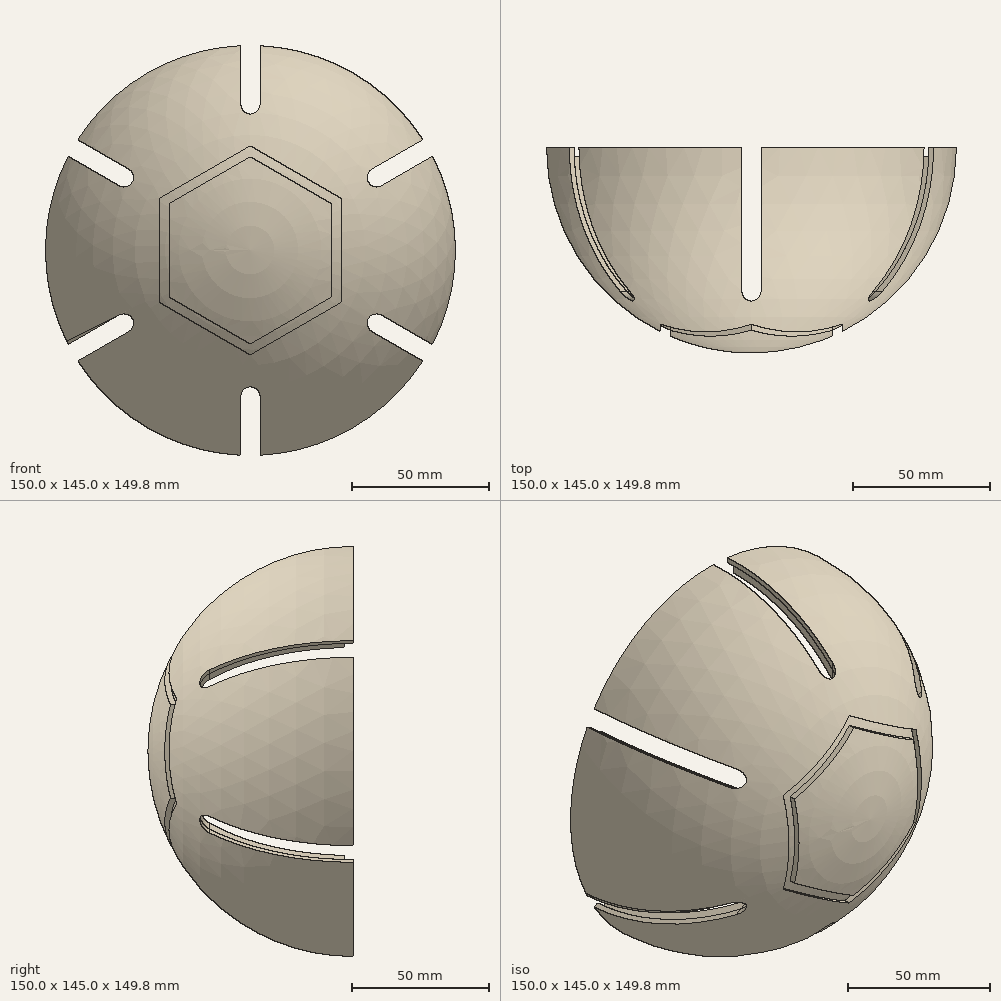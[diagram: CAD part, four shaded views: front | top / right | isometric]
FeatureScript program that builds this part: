
annotation { "Feature Type Name" : "Feature", "Feature Type Description" : "" }
export const myFeature = defineFeature(function(context is Context, id is Id, definition is map)
    precondition{}
    {
        {
            var Q0;
            Q0=qCreatedBy(makeId("Top.planeOp"),FACE);
            var sketch = newSketch(context, id + "F0", { "sketchPlane" : qUnion([Q0])});
            skArc(sketch, "E0", {"start": v(-75, 0) * mm, "mid": v(-53.03, -53.03) * mm, "end": v(0, -75) * mm});
            skLineSegment(sketch, "E1", {"start": v(0, 0) * mm, "end": v(-75, 0) * mm});
            skLineSegment(sketch, "E2", {"start": v(0, 0) * mm, "end": v(0, -75) * mm});
            skSolve(sketch);
        }
        {
            var Q0;
            Q0=makeQuery(id+"F0.imprint","IMPRINT",FACE,{"disambiguationData":[TD([[makeQuery(id+"F0.imprint","IMPRINT",EDGE,{"derivedFrom":sQuery(id+"F0.wireOp",EDGE,"E0")}),1.0]])]});
            var Q1;
            Q1=sQuery(id+"F0.wireOp",EDGE,"E2");
            var Q2;
            Q2=sQuery(id+"F0.wireOp",EDGE,"E2");
            revolve(context, id + "F1", {"entities" : qUnion([Q0]), "surfaceEntities" : qUnion([Q1]), "axis" : qUnion([Q2]), "revolveType" : RevolveType.FULL});
        }
        {
            var Q0;
            Q0=qCreatedBy(makeId("Top.planeOp"),FACE);
            var sketch = newSketch(context, id + "F2", { "sketchPlane" : qUnion([Q0])});
            skLineSegment(sketch, "E3", {"start": v(0, 0) * mm, "end": v(73, 0) * mm});
            skLineSegment(sketch, "E4", {"start": v(0, 0) * mm, "end": v(0, -73) * mm});
            skArc(sketch, "E5", {"start": v(0, -73) * mm, "mid": v(51.62, -51.62) * mm, "end": v(73, 0) * mm});
            skSolve(sketch);
        }
        {
            var Q0;
            Q0 = qSketchRegion(id + "F2", true);
            var Q1;
            Q1=sQuery(id+"F2.wireOp",EDGE,"E4");
            revolve(context, id + "F3", {"operationType" : NewBodyOperationType.REMOVE, "entities" : qUnion([Q0]), "axis" : qUnion([Q1]), "revolveType" : RevolveType.FULL, "oppositeDirection" : true});
        }
        {
            var Q0;
            Q0=qCreatedBy(makeId("Top.planeOp"),FACE);
            var sketch = newSketch(context, id + "F4", { "sketchPlane" : qUnion([Q0])});
            skLineSegment(sketch, "E6", {"start": v(3.5, -52.5) * mm, "end": v(3.5, 0) * mm});
            skLineSegment(sketch, "E7", {"start": v(-3.5, -52.5) * mm, "end": v(-3.5, 0) * mm});
            skLineSegment(sketch, "E8", {"start": v(3.5, 0) * mm, "end": v(-3.5, 0) * mm});
            skArc(sketch, "E9", {"start": v(-3.5, -52.5) * mm, "mid": v(0, -56) * mm, "end": v(3.5, -52.5) * mm});
            skSolve(sketch);
        }
        {
            var Q0;
            Q0=qCreatedBy(makeId("Front.planeOp"),FACE);
            cPlane(context, id + "F5", {"entities" : qUnion([Q0]), "cplaneType" : CPlaneType.OFFSET, "offset" : 88 * mm, "width" : 150 * mm, "height" : 150 * mm});
        }
        {
            var Q0;
            Q0=qCreatedBy(id+"F5.planeOp",FACE);
            var sketch = newSketch(context, id + "F6", { "sketchPlane" : qUnion([Q0])});
            skLineSegment(sketch, "E10.0", {"start": v(0, 38.25) * mm, "end": v(33.13, 19.13) * mm});
            skLineSegment(sketch, "E10.1", {"start": v(33.13, 19.13) * mm, "end": v(33.13, -19.13) * mm});
            skLineSegment(sketch, "E10.2", {"start": v(33.13, -19.13) * mm, "end": v(0, -38.25) * mm});
            skLineSegment(sketch, "E10.3", {"start": v(0, -38.25) * mm, "end": v(-33.13, -19.13) * mm});
            skLineSegment(sketch, "E10.4", {"start": v(-33.13, -19.13) * mm, "end": v(-33.13, 19.13) * mm});
            skLineSegment(sketch, "E10.5", {"start": v(-33.13, 19.13) * mm, "end": v(0, 38.25) * mm});
            skLineSegment(sketch, "E11.0", {"start": v(0, 34.25) * mm, "end": v(29.66, 17.13) * mm});
            skLineSegment(sketch, "E11.1", {"start": v(29.66, 17.13) * mm, "end": v(29.66, -17.13) * mm});
            skLineSegment(sketch, "E11.2", {"start": v(29.66, -17.13) * mm, "end": v(0, -34.25) * mm});
            skLineSegment(sketch, "E11.3", {"start": v(0, -34.25) * mm, "end": v(-29.66, -17.13) * mm});
            skLineSegment(sketch, "E11.4", {"start": v(-29.66, -17.13) * mm, "end": v(-29.66, 17.13) * mm});
            skLineSegment(sketch, "E11.5", {"start": v(-29.66, 17.13) * mm, "end": v(0, 34.25) * mm});
            skSolve(sketch);
        }
        {
            var Q0;
            Q0 = qSketchRegion(id + "F6", true);
            extrude(context, id + "F7", {"entities" : qUnion([Q0]), "operationType" : NewBodyOperationType.REMOVE, "oppositeDirection" : true, "depth" : 82.8 * mm});
        }
        {
            var Q0;
            Q0=qCreatedBy(makeId("Front.planeOp"),FACE);
            cPlane(context, id + "F8", {"entities" : qUnion([Q0]), "cplaneType" : CPlaneType.OFFSET, "offset" : 57.5 * mm, "width" : 150 * mm, "height" : 150 * mm});
        }
        {
            var Q0;
            Q0=qCreatedBy(makeId("Top.planeOp"),FACE);
            var sketch = newSketch(context, id + "F9", { "sketchPlane" : qUnion([Q0])});
            skArc(sketch, "E12", {"start": v(-69.94, -3) * mm, "mid": v(-48.43, -50.55) * mm, "end": v(0, -70) * mm});
            skArc(sketch, "E13", {"start": v(-72.94, -3) * mm, "mid": v(-50.55, -52.67) * mm, "end": v(0, -73) * mm});
            skLineSegment(sketch, "E14", {"start": v(0, -70) * mm, "end": v(0, -73) * mm});
            skLineSegment(sketch, "E15", {"start": v(-72.94, -3) * mm, "end": v(-69.94, -3) * mm});
            skPoint(sketch, "E16.orphan", {"position": v(0, -3) * mm});
            skSolve(sketch);
        }
        {
            var Q0;
            Q0 = qSketchRegion(id + "F9", true);
            var Q1;
            Q1=sQuery(id+"F9.wireOp",EDGE,"E14");
            revolve(context, id + "F10", {"entities" : qUnion([Q0]), "axis" : qUnion([Q1]), "revolveType" : RevolveType.FULL});
        }
        {
            var Q0;
            Q0=makeQuery(id+"F7.boolean.opBoolean","COPY",EDGE,{"derivedFrom":makeQuery(id+"F7.opExtrude","SWEPT_EDGE",EDGE,{"disambiguationData":[OSD([sQuery(id+"F6.wireOp",EDGE,"E11.0"),sQuery(id+"F6.wireOp",EDGE,"E11.1")])]})});
            var Q1;
            Q1=makeQuery(id+"F7.boolean.opBoolean","COPY",EDGE,{"derivedFrom":makeQuery(id+"F7.opExtrude","SWEPT_EDGE",EDGE,{"disambiguationData":[OSD([sQuery(id+"F6.wireOp",EDGE,"E10.0"),sQuery(id+"F6.wireOp",EDGE,"E10.1")])]})});
            cPlane(context, id + "F11", {"entities" : qUnion([Q0, Q1]), "cplaneType" : CPlaneType.LINE_ANGLE, "offset" : 25 * mm, "angle" : 90 * degree, "width" : 150 * mm, "height" : 150 * mm});
        }
        {
            var Q0;
            Q0=qCreatedBy(id+"F11.planeOp",FACE);
            cPlane(context, id + "F12", {"entities" : qUnion([Q0]), "cplaneType" : CPlaneType.OFFSET, "offset" : 145 * mm, "oppositeDirection" : true, "width" : 150 * mm, "height" : 150 * mm});
        }
        {
            var Q0;
            Q0=qCreatedBy(id+"F12.planeOp",FACE);
            var sketch = newSketch(context, id + "F13", { "sketchPlane" : qUnion([Q0])});
            skLineSegment(sketch, "E17", {"start": v(52.5, 3.5) * mm, "end": v(0, 3.5) * mm});
            skLineSegment(sketch, "E18", {"start": v(52.5, -3.5) * mm, "end": v(0, -3.5) * mm});
            skLineSegment(sketch, "E19", {"start": v(0, 3.5) * mm, "end": v(0, -3.5) * mm});
            skArc(sketch, "E20", {"start": v(52.5, -3.5) * mm, "mid": v(56, 0) * mm, "end": v(52.5, 3.5) * mm});
            skSolve(sketch);
        }
        {
            var Q0;
            Q0 = qSketchRegion(id + "F13", true);
            extrude(context, id + "F14", {"entities" : qUnion([Q0]), "operationType" : NewBodyOperationType.REMOVE, "endBound" : BoundingType.THROUGH_ALL, "depth" : 283 * mm, "offsetDistance" : 25 * mm});
        }
        {
            var Q0;
            Q0=makeQuery(id+"F7.boolean.opBoolean","COPY",EDGE,{"derivedFrom":makeQuery(id+"F7.opExtrude","SWEPT_EDGE",EDGE,{"disambiguationData":[OSD([sQuery(id+"F6.wireOp",EDGE,"E11.1"),sQuery(id+"F6.wireOp",EDGE,"E11.2")])]})});
            var Q1;
            Q1=makeQuery(id+"F7.boolean.opBoolean","COPY",EDGE,{"derivedFrom":makeQuery(id+"F7.opExtrude","SWEPT_EDGE",EDGE,{"disambiguationData":[OSD([sQuery(id+"F6.wireOp",EDGE,"E10.1"),sQuery(id+"F6.wireOp",EDGE,"E10.2")])]})});
            cPlane(context, id + "F15", {"entities" : qUnion([Q0, Q1]), "cplaneType" : CPlaneType.LINE_ANGLE, "offset" : 25 * mm, "angle" : 90 * degree, "width" : 150 * mm, "height" : 150 * mm});
        }
        {
            var Q0;
            Q0=qCreatedBy(id+"F15.planeOp",FACE);
            cPlane(context, id + "F16", {"entities" : qUnion([Q0]), "cplaneType" : CPlaneType.OFFSET, "offset" : 70 * mm, "oppositeDirection" : true, "width" : 150 * mm, "height" : 150 * mm});
        }
        {
            var Q0;
            Q0=qCreatedBy(id+"F16.planeOp",FACE);
            var sketch = newSketch(context, id + "F17", { "sketchPlane" : qUnion([Q0])});
            skLineSegment(sketch, "E21", {"start": v(52.5, 3.5) * mm, "end": v(0, 3.5) * mm});
            skLineSegment(sketch, "E22", {"start": v(52.5, -3.5) * mm, "end": v(0, -3.5) * mm});
            skLineSegment(sketch, "E23", {"start": v(0, 3.5) * mm, "end": v(0, -3.5) * mm});
            skArc(sketch, "E24", {"start": v(52.5, -3.5) * mm, "mid": v(56, 0) * mm, "end": v(52.5, 3.5) * mm});
            skSolve(sketch);
        }
        {
            var Q0;
            Q0 = qSketchRegion(id + "F17", true);
            extrude(context, id + "F18", {"entities" : qUnion([Q0]), "operationType" : NewBodyOperationType.REMOVE, "endBound" : BoundingType.THROUGH_ALL, "depth" : 261 * mm, "offsetDistance" : 25 * mm});
        }
        {
            var Q0;
            Q0 = qSketchRegion(id + "F4", true);
            extrude(context, id + "F19", {"entities" : qUnion([Q0]), "operationType" : NewBodyOperationType.REMOVE, "endBound" : BoundingType.THROUGH_ALL, "oppositeDirection" : true, "depth" : 184.6 * mm, "offsetDistance" : 25 * mm});
        }
        {
            var Q0;
            Q0 = qSketchRegion(id + "F4", true);
            extrude(context, id + "F20", {"entities" : qUnion([Q0]), "operationType" : NewBodyOperationType.REMOVE, "endBound" : BoundingType.THROUGH_ALL, "depth" : 193.7 * mm, "offsetDistance" : 25 * mm});
        }
    });
